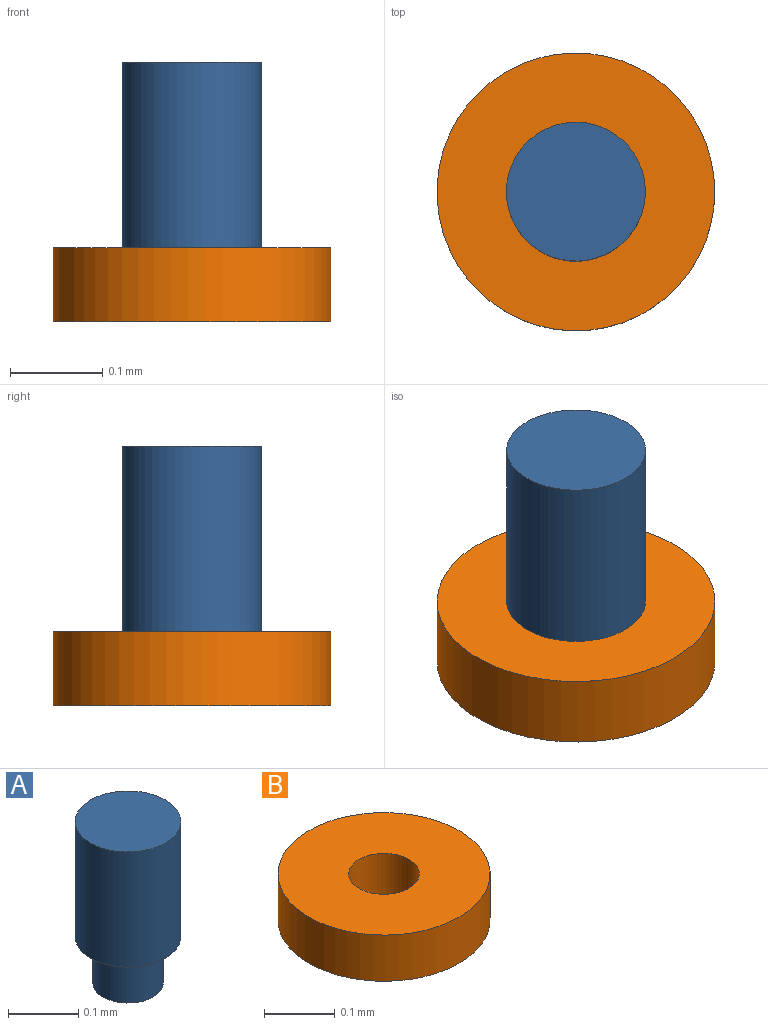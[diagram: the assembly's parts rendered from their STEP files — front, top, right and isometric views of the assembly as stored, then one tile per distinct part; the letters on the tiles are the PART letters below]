
ASSEMBLY  parts=2 mates=1
PART A: 5 faces, bbox 0.2x0.2x0.3 mm
  f0: plane 0.1x0.1mm, normal (0,0,-1), area 0mm2, adj f1
  f1: cylinder r=0.05mm len=0.1mm, axis (0,0,-1), area 0mm2, adj f0,f2
  f2: plane 0.15x0.15mm, normal (0,0,-1), area 0mm2, adj f1,f3
  f3: cylinder r=0.07mm len=0.2mm, axis (0,0,-1), area 0.1mm2, adj f2,f4
  f4: plane 0.15x0.15mm, normal (0,0,1), area 0mm2, adj f3
PART B: 4 faces, bbox 0.3x0.3x0.1 mm
  f0: cylinder r=0.05mm len=0.1mm, axis (0,0,-1), area 0mm2, adj f2,f3
  f1: cylinder r=0.15mm len=0.3mm, axis (0,0,-1), area 0.1mm2, adj f2,f3
  f2: plane 0.3x0.3mm, normal (0,0,1), area 0.1mm2, adj f0,f1
  f3: plane 0.3x0.3mm, normal (0,0,-1), area 0.1mm2, adj f0,f1
PLACE A t=(-0.1,-0.04,-0.02)mm
PLACE B t=(-0.1,-0.04,-0.02)mm
MATE revolute A.f1 <-> B.f0  axis (0,0,-1) through (-0.1,-0.04,-0.02)mm
